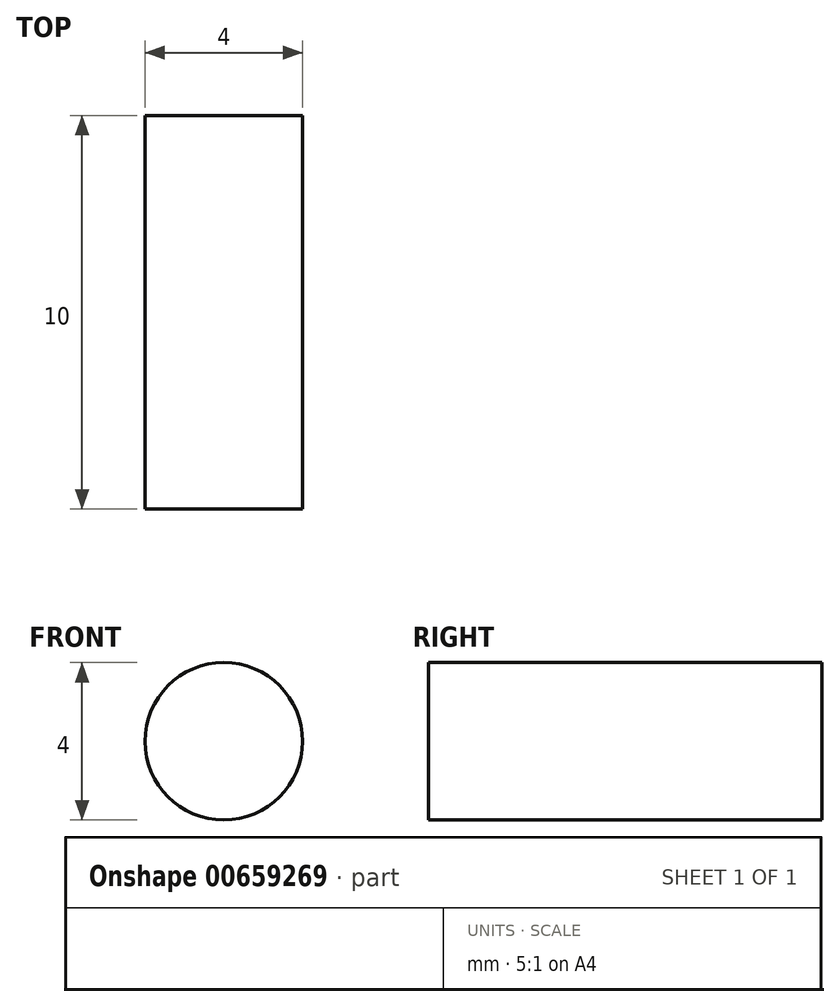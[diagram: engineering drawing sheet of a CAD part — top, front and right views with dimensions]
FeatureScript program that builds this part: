
annotation { "Feature Type Name" : "Feature", "Feature Type Description" : "" }
export const myFeature = defineFeature(function(context is Context, id is Id, definition is map)
    precondition{}
    {
        {
            var Q0;
            Q0=qCreatedBy(makeId("Top.planeOp"),FACE);
            var sketch = newSketch(context, id + "F0", { "sketchPlane" : qUnion([Q0])});
            skLineSegment(sketch, "E0.bottom", {"start": v(0, 0) * mm, "end": v(2, 0) * mm});
            skLineSegment(sketch, "E0.top", {"start": v(0, 10) * mm, "end": v(2, 10) * mm});
            skLineSegment(sketch, "E0.left", {"start": v(0, 0) * mm, "end": v(0, 10) * mm});
            skLineSegment(sketch, "E0.right", {"start": v(2, 0) * mm, "end": v(2, 10) * mm});
            skSolve(sketch);
        }
        {
            var Q0;
            Q0=makeQuery(id+"F0.imprint","IMPRINT",FACE,{"disambiguationData":[TD([[makeQuery(id+"F0.imprint","IMPRINT",EDGE,{"derivedFrom":sQuery(id+"F0.wireOp",EDGE,"E0.bottom")}),1.0]])]});
            var Q1;
            Q1=sQuery(id+"F0.wireOp",EDGE,"E0.left");
            revolve(context, id + "F1", {"entities" : qUnion([Q0]), "axis" : qUnion([Q1]), "revolveType" : RevolveType.FULL});
        }
    });
